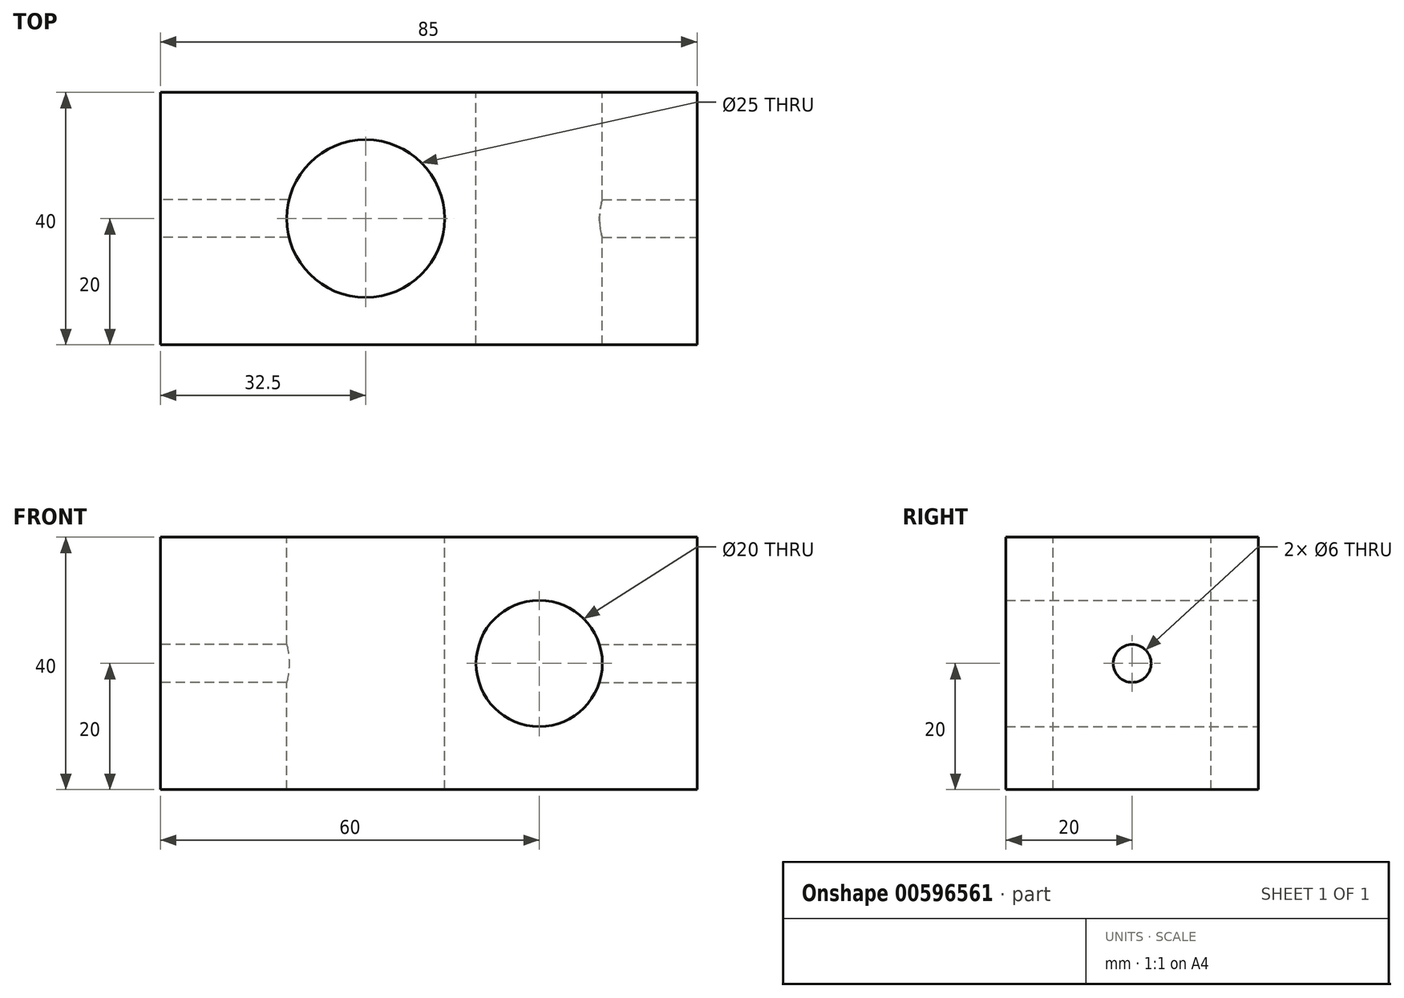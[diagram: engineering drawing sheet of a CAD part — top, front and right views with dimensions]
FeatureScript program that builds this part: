
annotation { "Feature Type Name" : "Feature", "Feature Type Description" : "" }
export const myFeature = defineFeature(function(context is Context, id is Id, definition is map)
    precondition{}
    {
        {
            var Q0;
            Q0=qCreatedBy(makeId("Front.planeOp"),FACE);
            var sketch = newSketch(context, id + "F0", { "sketchPlane" : qUnion([Q0])});
            skLineSegment(sketch, "E0.bottom", {"start": v(0, 0) * mm, "end": v(85, 0) * mm});
            skLineSegment(sketch, "E0.top", {"start": v(0, 40) * mm, "end": v(85, 40) * mm});
            skLineSegment(sketch, "E0.left", {"start": v(0, 0) * mm, "end": v(0, 40) * mm});
            skLineSegment(sketch, "E0.right", {"start": v(85, 0) * mm, "end": v(85, 40) * mm});
            skCircle(sketch, "E1", {"center": v(60, 20) * mm, "radius": 10 * mm});
            skSolve(sketch);
        }
        {
            var Q0;
            Q0=makeQuery(id+"F0.imprint","IMPRINT",FACE,{"disambiguationData":[TD([[makeQuery(id+"F0.imprint","IMPRINT",EDGE,{"derivedFrom":sQuery(id+"F0.wireOp",EDGE,"E0.bottom")}),1.0]])]});
            extrude(context, id + "F1", {"entities" : qUnion([Q0]), "depth" : 40 * mm, "offsetDistance" : 25 * mm});
        }
        {
            var Q0;
            Q0=makeQuery(id+"F1.opExtrude","SWEPT_FACE",FACE,{"disambiguationData":[OSD([sQuery(id+"F0.wireOp",EDGE,"E0.top")])]});
            var sketch = newSketch(context, id + "F2", { "sketchPlane" : qUnion([Q0])});
            skCircle(sketch, "E2", {"center": v(32.5, -20) * mm, "radius": 12.5 * mm});
            skPoint(sketch, "E2.centerSnap0", {"position": v(0, -20) * mm});
            skSolve(sketch);
        }
        {
            var Q0;
            Q0=makeQuery(id+"F2.imprint","IMPRINT",FACE,{"disambiguationData":[TD([[makeQuery(id+"F2.imprint","IMPRINT",EDGE,{"derivedFrom":sQuery(id+"F2.wireOp",EDGE,"E2")}),1.0]])]});
            extrude(context, id + "F3", {"entities" : qUnion([Q0]), "operationType" : NewBodyOperationType.REMOVE, "endBound" : BoundingType.THROUGH_ALL, "oppositeDirection" : true, "depth" : 25 * mm, "offsetDistance" : 25 * mm});
        }
        {
            var Q0;
            Q0=makeQuery(id+"F1.opExtrude","SWEPT_FACE",FACE,{"disambiguationData":[OSD([sQuery(id+"F0.wireOp",EDGE,"E0.right")])]});
            var sketch = newSketch(context, id + "F4", { "sketchPlane" : qUnion([Q0])});
            skCircle(sketch, "E3", {"center": v(-20, 20) * mm, "radius": 3 * mm});
            skPoint(sketch, "E3.centerSnap0", {"position": v(-20, 40) * mm});
            skPoint(sketch, "E3.centerSnap1", {"position": v(-40, 20) * mm});
            skSolve(sketch);
        }
        {
            var Q0;
            Q0=makeQuery(id+"F4.imprint","IMPRINT",FACE,{"disambiguationData":[TD([[makeQuery(id+"F4.imprint","IMPRINT",EDGE,{"derivedFrom":sQuery(id+"F4.wireOp",EDGE,"E3")}),1.0]])]});
            extrude(context, id + "F5", {"entities" : qUnion([Q0]), "operationType" : NewBodyOperationType.REMOVE, "oppositeDirection" : true, "depth" : 25 * mm, "offsetDistance" : 25 * mm});
        }
        {
            var Q0;
            Q0=makeQuery(id+"F1.opExtrude","SWEPT_FACE",FACE,{"disambiguationData":[OSD([sQuery(id+"F0.wireOp",EDGE,"E0.left")])]});
            var sketch = newSketch(context, id + "F6", { "sketchPlane" : qUnion([Q0])});
            skCircle(sketch, "E4", {"center": v(20, 20) * mm, "radius": 3 * mm});
            skPoint(sketch, "E4.centerSnap0", {"position": v(20, 40) * mm});
            skPoint(sketch, "E4.centerSnap1", {"position": v(0, 20) * mm});
            skSolve(sketch);
        }
        {
            var Q0;
            Q0=makeQuery(id+"F6.imprint","IMPRINT",FACE,{"disambiguationData":[TD([[makeQuery(id+"F6.imprint","IMPRINT",EDGE,{"derivedFrom":sQuery(id+"F6.wireOp",EDGE,"E4")}),1.0]])]});
            extrude(context, id + "F7", {"entities" : qUnion([Q0]), "operationType" : NewBodyOperationType.REMOVE, "oppositeDirection" : true, "depth" : 25 * mm, "offsetDistance" : 25 * mm});
        }
    });
